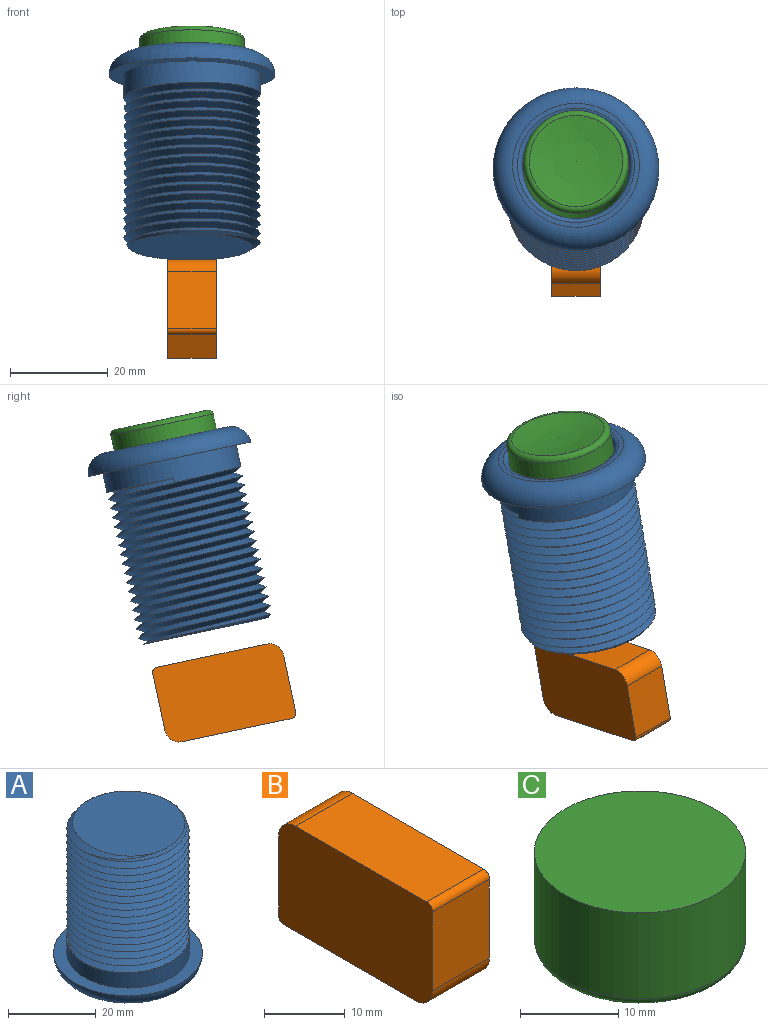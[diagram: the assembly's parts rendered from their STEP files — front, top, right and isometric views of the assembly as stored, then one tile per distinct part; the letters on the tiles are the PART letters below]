
ASSEMBLY  parts=3 mates=4
PART A: 14 faces, bbox 38.2x38.2x42.4 mm
  f0: plane 29.4x16.82mm, normal (0,0,1), area 37.6mm2, adj f1,f2,f4,f5
  f1: cylinder r=14mm len=28mm, axis (0,0,1), area 371.9mm2, adj f0,f2,f5,f9
  f2: plane 1.73x0.97mm, normal (0,1,0), area 0.9mm2, adj f0,f1,f3,f5
  f3: bspline ~33x32.21mm, area 2557.9mm2, adj f2,f4,f6,f7
  f4: bspline ~33.65x32.21mm, area 2607.7mm2, adj f0,f3,f5,f6,f7
  f5: bspline ~28x16.17mm, area 2.5mm2, adj f0,f1,f2,f4
  f6: cone r=13mm half-angle=45deg, axis (0,0,-1), area 31.6mm2, adj f3,f4,f7
  f7: plane 26.37x25.7mm, normal (0,0,1), area 518.1mm2, adj f3,f4,f6
  f8: plane 26x26mm, normal (0,0,-1), area 78.5mm2, adj f10,f13
  f9: plane 34x34mm, normal (0,0,1), area 292.2mm2, adj f1,f10
  f10: torus R=13mm, axis (0,0,-1), area 613.8mm2, adj f8,f9
  f11: cylinder r=11mm len=22mm, axis (0,0,-1), area 967.6mm2, adj f12,f13
  f12: plane 22x22mm, normal (0,0,-1), area 380.1mm2, adj f11
  f13: torus R=12mm, axis (0,0,-1), area 112.2mm2, adj f8,f11
PART B: 10 faces, bbox 10x27x16 mm
  f0: plane 23x10mm, normal (0,0,-1), area 230mm2, adj f4,f5,f7,f8
  f1: plane 12x10mm, normal (0,1,0), area 120mm2, adj f4,f5,f6,f8
  f2: plane 23x10mm, normal (0,0,1), area 230mm2, adj f4,f5,f6,f9
  f3: plane 12x10mm, normal (0,-1,0), area 120mm2, adj f4,f5,f7,f9
  f4: plane 27x16mm, normal (1,0,0), area 427.7mm2, adj f0,f1,f2,f3,f6,f7,f8,f9
  f5: plane 27x16mm, normal (-1,0,0), area 427.7mm2, adj f0,f1,f2,f3,f6,f7,f8,f9
  f6: cylinder r=3mm len=10mm, axis (1,0,0), area 47.1mm2, adj f1,f2,f4,f5
  f7: cylinder r=3mm len=10mm, axis (1,0,0), area 47.1mm2, adj f0,f3,f4,f5
  f8: cylinder r=1mm len=10mm, axis (-1,0,0), area 15.7mm2, adj f0,f1,f4,f5
  f9: cylinder r=1mm len=10mm, axis (-1,0,0), area 15.7mm2, adj f2,f3,f4,f5
PART C: 4 faces, bbox 23.3x23.3x11.7 mm
  f0: sphere r=54.96mm, area 290.3mm2, adj f3
  f1: cylinder r=10.75mm len=21.5mm, axis (0,0,-1), area 722.4mm2, adj f2,f3
  f2: plane 21.5x21.5mm, normal (0,0,1), area 363.1mm2, adj f1
  f3: torus R=9.75mm, axis (0,0,-1), area 113.1mm2, adj f0,f1
PLACE A rot(axis=(0,0.99,-0.1),180deg) t=(-126.16,193.14,-67.34)mm
PLACE B rot(axis=(0,0.99,-0.1),180deg) t=(-126.16,192.2,-67.35)mm
PLACE C rot(axis=(0,0.99,-0.1),180deg) t=(-126.16,193.22,-66.93)mm
MATE parallel B.f0 <-> A.f1  axis (0,0.21,0.98) through (-126.16,192.06,-72.43)mm
MATE cylindrical A.f1 <-> C.f1  axis (0,0.21,0.98) through (-126.16,201.21,-29.36)mm
MATE parallel B.f0 <-> A.f7  axis (0,0.21,0.98) through (-126.16,192.06,-72.43)mm
MATE cylindrical C.f1 <-> A.f1  axis (0,-0.21,-0.98) through (-126.16,202.33,-24.11)mm
